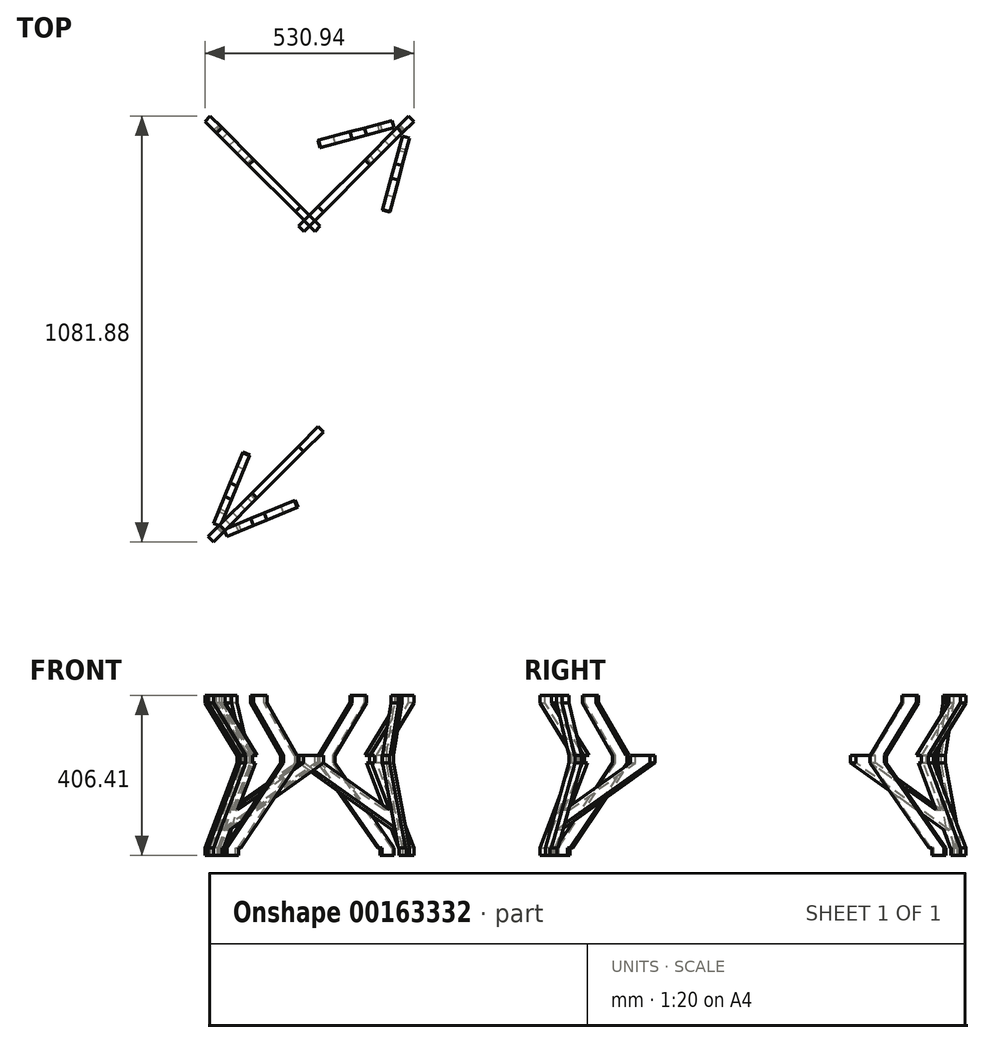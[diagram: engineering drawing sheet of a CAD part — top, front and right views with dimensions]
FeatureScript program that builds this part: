
annotation { "Feature Type Name" : "Feature", "Feature Type Description" : "" }
export const myFeature = defineFeature(function(context is Context, id is Id, definition is map)
    precondition{}
    {
        {
            var Q0;
            Q0=qCreatedBy(makeId("Top.planeOp"),FACE);
            var sketch = newSketch(context, id + "F0", { "sketchPlane" : qUnion([Q0])});
            skLineSegment(sketch, "E0.bottom", {"start": v(0, 1117.6) * mm, "end": v(558.8, 1117.6) * mm});
            skLineSegment(sketch, "E0.top", {"start": v(0, 0) * mm, "end": v(558.8, 0) * mm});
            skLineSegment(sketch, "E0.left", {"start": v(0, 1117.6) * mm, "end": v(0, 0) * mm});
            skLineSegment(sketch, "E0.right", {"start": v(558.8, 1117.6) * mm, "end": v(558.8, 0) * mm});
            skLineSegment(sketch, "E1", {"start": v(0, 0) * mm, "end": v(425.13, 425.13) * mm, "construction": true});
            skLineSegment(sketch, "E2", {"start": v(0, 1117.6) * mm, "end": v(422.37, 695.23) * mm, "construction": true});
            skLineSegment(sketch, "E3", {"start": v(558.8, 1117.6) * mm, "end": v(139.7, 698.5) * mm, "construction": true});
            skLineSegment(sketch, "E4", {"start": v(0, 1117.6) * mm, "end": v(139.7, 1117.6) * mm});
            skLineSegment(sketch, "E5", {"start": v(139.7, 1117.6) * mm, "end": v(139.7, 0) * mm, "construction": true});
            skLineSegment(sketch, "E6", {"start": v(558.8, 0) * mm, "end": v(419.1, 0) * mm});
            skLineSegment(sketch, "E7", {"start": v(558.8, 0) * mm, "end": v(436.13, 32.87) * mm});
            skLineSegment(sketch, "E8", {"start": v(558.8, 0) * mm, "end": v(525.93, 122.67) * mm});
            skLineSegment(sketch, "E9", {"start": v(436.13, 32.87) * mm, "end": v(525.93, 122.67) * mm});
            skLineSegment(sketch, "E10", {"start": v(525.93, 122.67) * mm, "end": v(497.46, 16.44) * mm, "construction": true});
            skLineSegment(sketch, "E11", {"start": v(436.13, 32.87) * mm, "end": v(542.37, 61.34) * mm, "construction": true});
            skLineSegment(sketch, "E12", {"start": v(558.8, 0) * mm, "end": v(540.82, 17.98) * mm});
            skLineSegment(sketch, "E13", {"start": v(511.63, 33.7) * mm, "end": v(525.1, 47.17) * mm});
            skLineSegment(sketch, "E14", {"start": v(525.1, 47.17) * mm, "end": v(547.55, 24.72) * mm});
            skLineSegment(sketch, "E15", {"start": v(547.55, 24.72) * mm, "end": v(534.08, 11.25) * mm});
            skLineSegment(sketch, "E16", {"start": v(534.08, 11.25) * mm, "end": v(511.63, 33.7) * mm});
            skLineSegment(sketch, "E17", {"start": v(436.13, 32.87) * mm, "end": v(460.66, 39.44) * mm});
            skLineSegment(sketch, "E18", {"start": v(460.66, 39.44) * mm, "end": v(458.2, 48.65) * mm});
            skLineSegment(sketch, "E19", {"start": v(458.2, 48.65) * mm, "end": v(488.86, 56.87) * mm});
            skLineSegment(sketch, "E20", {"start": v(488.86, 56.87) * mm, "end": v(493.8, 38.46) * mm});
            skLineSegment(sketch, "E21", {"start": v(493.8, 38.46) * mm, "end": v(463.12, 30.25) * mm});
            skLineSegment(sketch, "E22", {"start": v(460.66, 39.44) * mm, "end": v(463.12, 30.25) * mm});
            skLineSegment(sketch, "E23", {"start": v(525.93, 122.67) * mm, "end": v(519.36, 98.14) * mm});
            skLineSegment(sketch, "E24", {"start": v(510.15, 100.61) * mm, "end": v(528.56, 95.68) * mm});
            skLineSegment(sketch, "E25", {"start": v(528.56, 95.68) * mm, "end": v(520.34, 65) * mm});
            skLineSegment(sketch, "E26", {"start": v(520.34, 65) * mm, "end": v(501.93, 69.94) * mm});
            skLineSegment(sketch, "E27", {"start": v(501.93, 69.94) * mm, "end": v(510.15, 100.61) * mm});
            skLineSegment(sketch, "E28", {"start": v(558.8, 0) * mm, "end": v(139.7, 419.1) * mm, "construction": true});
            skLineSegment(sketch, "E29", {"start": v(558.8, 1117.6) * mm, "end": v(436.13, 1084.73) * mm});
            skLineSegment(sketch, "E30", {"start": v(558.8, 1117.6) * mm, "end": v(525.93, 994.93) * mm});
            skLineSegment(sketch, "E31", {"start": v(436.13, 1084.73) * mm, "end": v(525.93, 994.93) * mm});
            skLineSegment(sketch, "E32", {"start": v(544.69, 1090.11) * mm, "end": v(531.22, 1103.59) * mm});
            skLineSegment(sketch, "E33", {"start": v(531.22, 1103.59) * mm, "end": v(508.77, 1081.14) * mm});
            skLineSegment(sketch, "E34", {"start": v(508.77, 1081.14) * mm, "end": v(522.24, 1067.66) * mm});
            skLineSegment(sketch, "E35", {"start": v(522.24, 1067.66) * mm, "end": v(544.69, 1090.11) * mm});
            skLineSegment(sketch, "E36.0", {"start": v(551.72, 1115.7) * mm, "end": v(520.75, 1000.11) * mm, "construction": true});
            skLineSegment(sketch, "E37.0", {"start": v(443.2, 1086.63) * mm, "end": v(527.83, 1002) * mm, "construction": true});
            skLineSegment(sketch, "E38.trimOffspring", {"start": v(556.9, 1110.52) * mm, "end": v(441.31, 1079.55) * mm, "construction": true});
            skLineSegment(sketch, "E39", {"start": v(525.5, 1017.82) * mm, "end": v(507.09, 1022.75) * mm});
            skLineSegment(sketch, "E40", {"start": v(507.09, 1022.75) * mm, "end": v(515.3, 1053.41) * mm});
            skLineSegment(sketch, "E41", {"start": v(515.3, 1053.41) * mm, "end": v(533.7, 1048.48) * mm});
            skLineSegment(sketch, "E42", {"start": v(533.7, 1048.48) * mm, "end": v(525.5, 1017.82) * mm});
            skLineSegment(sketch, "E43", {"start": v(459, 1084.29) * mm, "end": v(463.94, 1065.9) * mm});
            skLineSegment(sketch, "E44", {"start": v(463.94, 1065.9) * mm, "end": v(494.6, 1074.11) * mm});
            skLineSegment(sketch, "E45", {"start": v(494.6, 1074.11) * mm, "end": v(489.68, 1092.5) * mm});
            skLineSegment(sketch, "E46", {"start": v(489.68, 1092.5) * mm, "end": v(459, 1084.29) * mm});
            skPoint(sketch, "E47", {"position": v(492.14, 1083.3) * mm});
            skPoint(sketch, "E48", {"position": v(524.5, 1050.95) * mm});
            skLineSegment(sketch, "E49", {"start": v(492.14, 1083.3) * mm, "end": v(139.7, 988.87) * mm, "construction": true});
            skLineSegment(sketch, "E50", {"start": v(516.29, 1020.29) * mm, "end": v(422.56, 670.5) * mm, "construction": true});
            skPoint(sketch, "E51.orphan", {"position": v(461.47, 1075.1) * mm});
            skLineSegment(sketch, "E52", {"start": v(0, 1117.6) * mm, "end": v(32.87, 994.93) * mm});
            skLineSegment(sketch, "E53", {"start": v(0, 1117.6) * mm, "end": v(122.67, 1084.73) * mm});
            skLineSegment(sketch, "E54", {"start": v(122.67, 1084.73) * mm, "end": v(32.87, 994.93) * mm});
            skLineSegment(sketch, "E55.0", {"start": v(6.57, 1117.6) * mm, "end": v(38.05, 1000.11) * mm, "construction": true});
            skLineSegment(sketch, "E56.0", {"start": v(0, 1111.03) * mm, "end": v(117.49, 1079.55) * mm, "construction": true});
            skLineSegment(sketch, "E57.0", {"start": v(115.6, 1086.63) * mm, "end": v(30.97, 1002) * mm, "construction": true});
            skLineSegment(sketch, "E58", {"start": v(33.3, 1017.85) * mm, "end": v(51.7, 1022.78) * mm});
            skLineSegment(sketch, "E59", {"start": v(51.7, 1022.78) * mm, "end": v(43.49, 1053.45) * mm});
            skLineSegment(sketch, "E60", {"start": v(43.49, 1053.45) * mm, "end": v(25.09, 1048.51) * mm});
            skLineSegment(sketch, "E61", {"start": v(25.09, 1048.51) * mm, "end": v(33.3, 1017.85) * mm});
            skLineSegment(sketch, "E62", {"start": v(99.77, 1084.3) * mm, "end": v(94.84, 1065.9) * mm});
            skLineSegment(sketch, "E63", {"start": v(94.84, 1065.9) * mm, "end": v(64.18, 1074.1) * mm});
            skLineSegment(sketch, "E64", {"start": v(64.18, 1074.1) * mm, "end": v(69.11, 1092.5) * mm});
            skLineSegment(sketch, "E65", {"start": v(69.11, 1092.5) * mm, "end": v(99.77, 1084.3) * mm});
            skPoint(sketch, "E66", {"position": v(66.65, 1083.3) * mm});
            skPoint(sketch, "E67", {"position": v(34.29, 1050.98) * mm});
            skLineSegment(sketch, "E68", {"start": v(66.65, 1083.3) * mm, "end": v(420.1, 988.6) * mm, "construction": true});
            skLineSegment(sketch, "E69", {"start": v(34.29, 1050.98) * mm, "end": v(139.7, 657.57) * mm, "construction": true});
            skPoint(sketch, "E70", {"position": v(419.1, 1117.6) * mm});
            skLineSegment(sketch, "E71", {"start": v(419.1, 1117.6) * mm, "end": v(427.75, 0) * mm, "construction": true});
            skLineSegment(sketch, "E72.MirrorCS", {"start": v(59.37, 1058.23) * mm, "end": v(-363, 1480.6) * mm, "construction": true});
            skLineSegment(sketch, "E73", {"start": v(27.38, 1103.69) * mm, "end": v(13.91, 1090.22) * mm});
            skLineSegment(sketch, "E74", {"start": v(13.91, 1090.22) * mm, "end": v(36.36, 1067.77) * mm});
            skLineSegment(sketch, "E75", {"start": v(36.36, 1067.77) * mm, "end": v(49.83, 1081.24) * mm});
            skLineSegment(sketch, "E76", {"start": v(27.38, 1103.69) * mm, "end": v(49.83, 1081.24) * mm});
            skLineSegment(sketch, "E77", {"start": v(0, 0) * mm, "end": v(48.6, 117.33) * mm});
            skLineSegment(sketch, "E78", {"start": v(0, 0) * mm, "end": v(117.33, 48.6) * mm});
            skPoint(sketch, "E79", {"position": v(117.33, 48.6) * mm});
            skPoint(sketch, "E80", {"position": v(48.6, 117.33) * mm});
            skLineSegment(sketch, "E81", {"start": v(48.6, 117.33) * mm, "end": v(117.33, 48.6) * mm});
            skLineSegment(sketch, "E82.0", {"start": v(5.87, -2.43) * mm, "end": v(54.47, 114.9) * mm, "construction": true});
            skLineSegment(sketch, "E83.0", {"start": v(-2.43, 5.87) * mm, "end": v(114.9, 54.47) * mm, "construction": true});
            skLineSegment(sketch, "E84", {"start": v(21.83, 35.3) * mm, "end": v(44.28, 57.75) * mm});
            skLineSegment(sketch, "E85", {"start": v(35.3, 21.83) * mm, "end": v(57.75, 44.28) * mm});
            skLineSegment(sketch, "E86", {"start": v(44.28, 57.75) * mm, "end": v(57.75, 44.28) * mm});
            skLineSegment(sketch, "E87", {"start": v(21.83, 35.3) * mm, "end": v(35.3, 21.83) * mm});
            skLineSegment(sketch, "E88.0", {"start": v(44.11, 112.84) * mm, "end": v(112.84, 44.11) * mm, "construction": true});
            skLineSegment(sketch, "E89", {"start": v(47.74, 98.66) * mm, "end": v(65.34, 91.37) * mm});
            skLineSegment(sketch, "E90", {"start": v(65.34, 91.37) * mm, "end": v(53.2, 62.04) * mm});
            skLineSegment(sketch, "E91", {"start": v(53.2, 62.04) * mm, "end": v(35.6, 69.33) * mm});
            skLineSegment(sketch, "E92", {"start": v(35.6, 69.33) * mm, "end": v(47.74, 98.66) * mm});
            skLineSegment(sketch, "E93", {"start": v(98.94, 47.85) * mm, "end": v(91.65, 65.45) * mm});
            skLineSegment(sketch, "E94", {"start": v(91.65, 65.45) * mm, "end": v(62.3, 53.3) * mm});
            skLineSegment(sketch, "E95", {"start": v(62.3, 53.3) * mm, "end": v(69.6, 35.7) * mm});
            skLineSegment(sketch, "E96", {"start": v(69.6, 35.7) * mm, "end": v(98.94, 47.85) * mm});
            skPoint(sketch, "E97", {"position": v(65.95, 44.5) * mm});
            skLineSegment(sketch, "E98", {"start": v(95.3, 56.65) * mm, "end": v(426.25, 193.74) * mm, "construction": true});
            skPoint(sketch, "E99", {"position": v(44.4, 65.69) * mm});
            skLineSegment(sketch, "E100", {"start": v(44.4, 65.69) * mm, "end": v(139.7, 295.78) * mm, "construction": true});
            skPoint(sketch, "E101.orphan", {"position": v(56.54, 95.02) * mm});
            skSolve(sketch);
        }
        {
            var Q0;
            Q0=sQuery(id+"F0.wireOp",EDGE,"E1");
            var Q1;
            {var subQ1=sQuery(id+"F0.wireOp",EDGE,"E1");var subQ7=sQuery(id+"F0.wireOp",EDGE,"E5");var subQ9=makeQuery(id+"F0.imprint","INTERSECT",VERTEX,{"derivedFrom":[subQ1,subQ7]});Q1=makeQuery(id+"F0.imprint","IMPRINT",FACE,{"disambiguationData":[TD([[makeQuery(id+"F0.imprint","IMPRINT",EDGE,{"disambiguationData":[TD([[subQ9,-1.0]])],"derivedFrom":subQ1}),-1.0]])]});}
            cPlane(context, id + "F1", {"entities" : qUnion([Q0, Q1]), "cplaneType" : CPlaneType.LINE_ANGLE, "offset" : 25.4 * mm, "angle" : 90 * degree, "width" : 152.4 * mm, "height" : 152.4 * mm});
        }
        {
            var Q0;
            Q0=sQuery(id+"F0.wireOp",EDGE,"E3");
            var Q1;
            {var subQ0=sQuery(id+"F0.wireOp",EDGE,"E5");var subQ1=sQuery(id+"F0.wireOp",EDGE,"E2");var subQ2=makeQuery(id+"F0.imprint","INTERSECT",VERTEX,{"derivedFrom":[subQ1,subQ0]});Q1=makeQuery(id+"F0.imprint","IMPRINT",FACE,{"disambiguationData":[TD([[makeQuery(id+"F0.imprint","IMPRINT",EDGE,{"disambiguationData":[TD([[subQ2,-1.0]])],"derivedFrom":subQ1}),-1.0]])]});}
            cPlane(context, id + "F2", {"entities" : qUnion([Q0, Q1]), "cplaneType" : CPlaneType.LINE_ANGLE, "offset" : 25.4 * mm, "angle" : 90 * degree, "width" : 152.4 * mm, "height" : 152.4 * mm});
        }
        {
            var Q0;
            Q0=qCreatedBy(id+"F2.planeOp",FACE);
            var sketch = newSketch(context, id + "F3", { "sketchPlane" : qUnion([Q0])});
            skLineSegment(sketch, "E102", {"start": v(1156.11, 0) * mm, "end": v(1156.11, 406.4) * mm, "construction": true});
            skLineSegment(sketch, "E103", {"start": v(592.65, 0) * mm, "end": v(592.65, 406.4) * mm, "construction": true});
            skLineSegment(sketch, "E104", {"start": v(1156.11, 406.4) * mm, "end": v(592.65, 406.4) * mm, "construction": true});
            skLineSegment(sketch, "E105.0", {"start": v(1156.11, 387.35) * mm, "end": v(592.65, 387.35) * mm, "construction": true});
            skPoint(sketch, "E106", {"position": v(1156.11, 254) * mm});
            skLineSegment(sketch, "E107", {"start": v(1156.11, 254) * mm, "end": v(592.65, 254) * mm, "construction": true});
            skLineSegment(sketch, "E108.0", {"start": v(1156.11, 234.95) * mm, "end": v(1040.74, 234.95) * mm, "construction": true});
            skLineSegment(sketch, "E109", {"start": v(1124.36, 0) * mm, "end": v(592.65, 0) * mm, "construction": true});
            skLineSegment(sketch, "E110.0", {"start": v(1120, 19.05) * mm, "end": v(592.65, 19.05) * mm, "construction": true});
            skLineSegment(sketch, "E111", {"start": v(1156.11, 19.05) * mm, "end": v(1040.74, 234.95) * mm});
            skLineSegment(sketch, "E112", {"start": v(1124.36, 19.05) * mm, "end": v(1124.36, 0) * mm});
            skLineSegment(sketch, "E113", {"start": v(1120, 19.05) * mm, "end": v(1094.73, 66.36) * mm});
            skLineSegment(sketch, "E114", {"start": v(1040.74, 234.95) * mm, "end": v(1040.74, 254) * mm});
            skLineSegment(sketch, "E115", {"start": v(1040.74, 254) * mm, "end": v(1156.11, 387.35) * mm});
            skLineSegment(sketch, "E116", {"start": v(1124.36, 19.05) * mm, "end": v(1120, 19.05) * mm});
            skLineSegment(sketch, "E117.0", {"start": v(998.76, 254) * mm, "end": v(1114.13, 387.35) * mm});
            skLineSegment(sketch, "E118", {"start": v(1015.34, 234.95) * mm, "end": v(1015.34, 254) * mm});
            skLineSegment(sketch, "E119", {"start": v(1015.34, 254) * mm, "end": v(998.76, 254) * mm});
            skLineSegment(sketch, "E120", {"start": v(1015.34, 234.95) * mm, "end": v(1004.64, 234.95) * mm});
            skLineSegment(sketch, "E121", {"start": v(1094.73, 66.36) * mm, "end": v(760.94, 234.95) * mm});
            skLineSegment(sketch, "E122.0", {"start": v(1068.7, 115.08) * mm, "end": v(831.36, 234.95) * mm});
            skLineSegment(sketch, "E123.trimOffspring", {"start": v(1068.7, 115.08) * mm, "end": v(1004.64, 234.95) * mm});
            skLineSegment(sketch, "E124", {"start": v(790.12, 0) * mm, "end": v(779.62, 406.4) * mm, "construction": true});
            skLineSegment(sketch, "E125", {"start": v(760.94, 234.95) * mm, "end": v(760.94, 254) * mm});
            skLineSegment(sketch, "E126", {"start": v(831.36, 234.95) * mm, "end": v(831.36, 254) * mm});
            skLineSegment(sketch, "E127", {"start": v(831.36, 254) * mm, "end": v(760.94, 254) * mm});
            skLineSegment(sketch, "E128", {"start": v(1004.64, 234.95) * mm, "end": v(1015.34, 234.95) * mm});
            skLineSegment(sketch, "E129.trimOffspring", {"start": v(1015.34, 234.95) * mm, "end": v(592.65, 234.95) * mm, "construction": true});
            skLineSegment(sketch, "E130", {"start": v(1156.11, 19.05) * mm, "end": v(1156.11, 0) * mm});
            skLineSegment(sketch, "E131", {"start": v(1156.11, 0) * mm, "end": v(1124.36, 0) * mm});
            skLineSegment(sketch, "E132", {"start": v(1114.13, 387.35) * mm, "end": v(1114.13, 406.4) * mm});
            skLineSegment(sketch, "E133", {"start": v(1114.13, 406.4) * mm, "end": v(1156.11, 406.4) * mm});
            skLineSegment(sketch, "E134", {"start": v(1156.11, 387.35) * mm, "end": v(1156.11, 406.4) * mm});
            skSolve(sketch);
        }
        {
            var Q0;
            Q0=sQuery(id+"F0.wireOp",EDGE,"E49");
            cPlane(context, id + "F4", {"entities" : qUnion([Q0]), "cplaneType" : CPlaneType.LINE_ANGLE, "offset" : 25.4 * mm, "angle" : 180 * degree, "width" : 152.4 * mm, "height" : 152.4 * mm});
        }
        {
            var Q0;
            Q0=qCreatedBy(id+"F4.planeOp",FACE);
            var sketch = newSketch(context, id + "F5", { "sketchPlane" : qUnion([Q0])});
            skLineSegment(sketch, "E135", {"start": v(-755.76, 0) * mm, "end": v(-755.76, 406.4) * mm, "construction": true});
            skLineSegment(sketch, "E136", {"start": v(-390.89, 0) * mm, "end": v(-390.89, 406.4) * mm, "construction": true});
            skLineSegment(sketch, "E137", {"start": v(-535.5, 0) * mm, "end": v(-535.5, 406.4) * mm, "construction": true});
            skLineSegment(sketch, "E138", {"start": v(-755.76, 406.4) * mm, "end": v(-682.75, 406.4) * mm, "construction": true});
            skLineSegment(sketch, "E139", {"start": v(-755.76, 254) * mm, "end": v(-390.89, 254) * mm, "construction": true});
            skLineSegment(sketch, "E140", {"start": v(-755.76, 0) * mm, "end": v(-390.89, 0) * mm, "construction": true});
            skLineSegment(sketch, "E141.0", {"start": v(-755.76, 387.35) * mm, "end": v(-390.89, 387.35) * mm, "construction": true});
            skLineSegment(sketch, "E142.0", {"start": v(-803.66, 234.95) * mm, "end": v(-315.69, 234.95) * mm, "construction": true});
            skLineSegment(sketch, "E143", {"start": v(-755.76, 0) * mm, "end": v(-724.01, 0) * mm});
            skLineSegment(sketch, "E144", {"start": v(-724.01, 0) * mm, "end": v(-724.01, 19.05) * mm});
            skLineSegment(sketch, "E145", {"start": v(-755.76, 19.05) * mm, "end": v(-755.76, 0) * mm});
            skLineSegment(sketch, "E146", {"start": v(-755.76, 19.05) * mm, "end": v(-599.6, 234.95) * mm});
            skLineSegment(sketch, "E147.0", {"start": v(-716.58, 19.05) * mm, "end": v(-560.41, 234.95) * mm});
            skLineSegment(sketch, "E148", {"start": v(-724.01, 19.05) * mm, "end": v(-716.58, 19.05) * mm});
            skLineSegment(sketch, "E149", {"start": v(-599.6, 234.95) * mm, "end": v(-599.6, 254) * mm});
            skLineSegment(sketch, "E150", {"start": v(-560.41, 234.95) * mm, "end": v(-560.41, 254) * mm});
            skLineSegment(sketch, "E151", {"start": v(-599.6, 254) * mm, "end": v(-682.75, 387.35) * mm});
            skLineSegment(sketch, "E152.0", {"start": v(-562.18, 254) * mm, "end": v(-645.33, 387.35) * mm});
            skLineSegment(sketch, "E153", {"start": v(-682.75, 387.35) * mm, "end": v(-682.75, 406.4) * mm});
            skLineSegment(sketch, "E154", {"start": v(-645.33, 387.35) * mm, "end": v(-645.33, 406.4) * mm});
            skLineSegment(sketch, "E155.trimOffspring", {"start": v(-639.62, 406.4) * mm, "end": v(-390.89, 406.4) * mm, "construction": true});
            skLineSegment(sketch, "E156", {"start": v(-682.75, 406.4) * mm, "end": v(-645.33, 406.4) * mm});
            skLineSegment(sketch, "E157", {"start": v(-562.18, 254) * mm, "end": v(-560.41, 254) * mm});
            skSolve(sketch);
        }
        {
            var Q0;
            Q0=makeQuery(id+"F3.imprint","IMPRINT",FACE,{"disambiguationData":[TD([[makeQuery(id+"F3.imprint","IMPRINT",EDGE,{"derivedFrom":sQuery(id+"F3.wireOp",EDGE,"E111")}),1.0]])]});
            extrude(context, id + "F6", {"entities" : qUnion([Q0]), "endBound" : BoundingType.SYMMETRIC, "depth" : 19.05 * mm});
        }
        {
            var Q0;
            Q0=makeQuery(id+"F5.imprint","IMPRINT",FACE,{"disambiguationData":[TD([[makeQuery(id+"F5.imprint","IMPRINT",EDGE,{"derivedFrom":sQuery(id+"F5.wireOp",EDGE,"E143")}),1.0]])]});
            extrude(context, id + "F7", {"entities" : qUnion([Q0]), "endBound" : BoundingType.SYMMETRIC, "depth" : 19.05 * mm});
        }
        {
            var Q0;
            Q0=sQuery(id+"F0.wireOp",EDGE,"E50");
            cPlane(context, id + "F8", {"entities" : qUnion([Q0]), "cplaneType" : CPlaneType.LINE_ANGLE, "offset" : 25.4 * mm, "angle" : 90 * degree, "width" : 152.4 * mm, "height" : 152.4 * mm});
        }
        {
            var Q0;
            Q0=qCreatedBy(id+"F8.planeOp",FACE);
            var sketch = newSketch(context, id + "F9", { "sketchPlane" : qUnion([Q0])});
            skLineSegment(sketch, "E158", {"start": v(786.02, 0) * mm, "end": v(786.02, 406.4) * mm, "construction": true});
            skLineSegment(sketch, "E159.MirrorCS", {"start": v(957.31, 254) * mm, "end": v(955.54, 254) * mm});
            skLineSegment(sketch, "E160.MirrorCS", {"start": v(1119.14, 19.06) * mm, "end": v(1111.7, 19.06) * mm});
            skLineSegment(sketch, "E161.MirrorCS", {"start": v(1150.9, 19.06) * mm, "end": v(1150.9, 0) * mm});
            skLineSegment(sketch, "E162.MirrorCS", {"start": v(1119.14, 0) * mm, "end": v(1119.14, 19.06) * mm});
            skLineSegment(sketch, "E163.MirrorCS", {"start": v(1150.9, 0) * mm, "end": v(1119.14, 0) * mm});
            skLineSegment(sketch, "E164.MirrorCS", {"start": v(1034.75, 406.4) * mm, "end": v(786.02, 406.4) * mm, "construction": true});
            skLineSegment(sketch, "E165.MirrorCS", {"start": v(994.73, 254) * mm, "end": v(1077.87, 387.36) * mm});
            skLineSegment(sketch, "E166.MirrorCS", {"start": v(1077.87, 387.36) * mm, "end": v(1077.87, 406.4) * mm});
            skLineSegment(sketch, "E167.MirrorCS", {"start": v(1111.7, 19.06) * mm, "end": v(955.54, 234.96) * mm});
            skLineSegment(sketch, "E168.MirrorCS", {"start": v(1150.9, 19.06) * mm, "end": v(994.73, 234.96) * mm});
            skLineSegment(sketch, "E169.MirrorCS", {"start": v(1040.46, 387.36) * mm, "end": v(1040.46, 406.4) * mm});
            skLineSegment(sketch, "E170.MirrorCS", {"start": v(1150.9, 234.96) * mm, "end": v(786.02, 234.96) * mm, "construction": true});
            skLineSegment(sketch, "E171.MirrorCS", {"start": v(1077.87, 406.4) * mm, "end": v(1040.46, 406.4) * mm});
            skLineSegment(sketch, "E172.MirrorCS", {"start": v(1150.9, 387.36) * mm, "end": v(786.02, 387.36) * mm, "construction": true});
            skLineSegment(sketch, "E173.MirrorCS", {"start": v(1150.9, 0) * mm, "end": v(786.02, 0) * mm, "construction": true});
            skLineSegment(sketch, "E174.MirrorCS", {"start": v(1150.9, 254) * mm, "end": v(786.02, 254) * mm, "construction": true});
            skLineSegment(sketch, "E175.MirrorCS", {"start": v(1150.9, 406.4) * mm, "end": v(1077.87, 406.4) * mm, "construction": true});
            skLineSegment(sketch, "E176.MirrorCS", {"start": v(1150.9, 0) * mm, "end": v(1150.9, 406.4) * mm, "construction": true});
            skLineSegment(sketch, "E177.MirrorCS", {"start": v(930.63, 0) * mm, "end": v(930.63, 406.4) * mm, "construction": true});
            skLineSegment(sketch, "E178.MirrorCS", {"start": v(955.54, 234.96) * mm, "end": v(955.54, 254) * mm});
            skLineSegment(sketch, "E179.MirrorCS", {"start": v(994.73, 234.96) * mm, "end": v(994.73, 254) * mm});
            skLineSegment(sketch, "E180.MirrorCS", {"start": v(957.31, 254) * mm, "end": v(1040.46, 387.36) * mm});
            skSolve(sketch);
        }
        {
            var Q0;
            Q0=makeQuery(id+"F9.imprint","IMPRINT",FACE,{"disambiguationData":[TD([[makeQuery(id+"F9.imprint","IMPRINT",EDGE,{"derivedFrom":sQuery(id+"F9.wireOp",EDGE,"E159.MirrorCS")}),1.0]])]});
            extrude(context, id + "F10", {"entities" : qUnion([Q0]), "endBound" : BoundingType.SYMMETRIC, "depth" : 19.05 * mm});
        }
        {
            var Q0;
            Q0=sQuery(id+"F0.wireOp",EDGE,"E2");
            cPlane(context, id + "F11", {"entities" : qUnion([Q0]), "cplaneType" : CPlaneType.LINE_ANGLE, "offset" : 25.4 * mm, "angle" : 90 * degree, "width" : 152.4 * mm, "height" : 152.4 * mm});
        }
        {
            var Q0;
            Q0=qCreatedBy(id+"F11.planeOp",FACE);
            var sketch = newSketch(context, id + "F12", { "sketchPlane" : qUnion([Q0])});
            skLineSegment(sketch, "E181", {"start": v(761.1, 0) * mm, "end": v(761.1, 406.4) * mm, "construction": true});
            skLineSegment(sketch, "E182", {"start": v(197.63, 0) * mm, "end": v(197.63, 406.4) * mm, "construction": true});
            skLineSegment(sketch, "E183", {"start": v(761.1, 406.4) * mm, "end": v(197.63, 406.4) * mm, "construction": true});
            skLineSegment(sketch, "E184.0", {"start": v(761.1, 387.35) * mm, "end": v(197.63, 387.35) * mm, "construction": true});
            skPoint(sketch, "E185", {"position": v(761.1, 254) * mm});
            skLineSegment(sketch, "E186", {"start": v(761.1, 254) * mm, "end": v(197.63, 254) * mm, "construction": true});
            skLineSegment(sketch, "E187.0", {"start": v(761.1, 234.95) * mm, "end": v(645.72, 234.95) * mm, "construction": true});
            skLineSegment(sketch, "E188", {"start": v(729.34, 0) * mm, "end": v(197.63, 0) * mm, "construction": true});
            skLineSegment(sketch, "E189.0", {"start": v(724.99, 19.05) * mm, "end": v(197.63, 19.05) * mm, "construction": true});
            skLineSegment(sketch, "E190", {"start": v(761.1, 19.05) * mm, "end": v(645.72, 234.95) * mm});
            skLineSegment(sketch, "E191", {"start": v(729.34, 19.05) * mm, "end": v(729.34, 0) * mm});
            skLineSegment(sketch, "E192", {"start": v(724.99, 19.05) * mm, "end": v(699.7, 66.36) * mm});
            skLineSegment(sketch, "E193", {"start": v(645.72, 234.95) * mm, "end": v(645.72, 254) * mm});
            skLineSegment(sketch, "E194", {"start": v(645.72, 254) * mm, "end": v(761.1, 387.35) * mm});
            skLineSegment(sketch, "E195", {"start": v(729.34, 19.05) * mm, "end": v(724.99, 19.05) * mm});
            skLineSegment(sketch, "E196.0", {"start": v(603.73, 254) * mm, "end": v(719.1, 387.35) * mm});
            skLineSegment(sketch, "E197", {"start": v(620.32, 234.95) * mm, "end": v(620.32, 254) * mm});
            skLineSegment(sketch, "E198", {"start": v(620.32, 254) * mm, "end": v(603.73, 254) * mm});
            skLineSegment(sketch, "E199", {"start": v(620.32, 234.95) * mm, "end": v(609.61, 234.95) * mm});
            skLineSegment(sketch, "E200", {"start": v(699.7, 66.36) * mm, "end": v(365.91, 234.95) * mm});
            skLineSegment(sketch, "E201.0", {"start": v(673.67, 115.08) * mm, "end": v(436.34, 234.95) * mm});
            skLineSegment(sketch, "E202.trimOffspring", {"start": v(673.67, 115.08) * mm, "end": v(609.61, 234.95) * mm});
            skLineSegment(sketch, "E203", {"start": v(395.1, 0) * mm, "end": v(384.6, 406.4) * mm, "construction": true});
            skLineSegment(sketch, "E204", {"start": v(365.91, 234.95) * mm, "end": v(365.91, 254) * mm});
            skLineSegment(sketch, "E205", {"start": v(436.34, 234.95) * mm, "end": v(436.34, 254) * mm});
            skLineSegment(sketch, "E206", {"start": v(436.34, 254) * mm, "end": v(365.91, 254) * mm});
            skLineSegment(sketch, "E207", {"start": v(609.61, 234.95) * mm, "end": v(620.32, 234.95) * mm});
            skLineSegment(sketch, "E208.trimOffspring", {"start": v(620.32, 234.95) * mm, "end": v(197.63, 234.95) * mm, "construction": true});
            skLineSegment(sketch, "E209", {"start": v(761.1, 19.05) * mm, "end": v(761.1, 0) * mm});
            skLineSegment(sketch, "E210", {"start": v(761.1, 0) * mm, "end": v(729.34, 0) * mm});
            skLineSegment(sketch, "E211", {"start": v(719.1, 387.35) * mm, "end": v(719.1, 406.4) * mm});
            skLineSegment(sketch, "E212", {"start": v(719.1, 406.4) * mm, "end": v(761.1, 406.4) * mm});
            skLineSegment(sketch, "E213", {"start": v(761.1, 387.35) * mm, "end": v(761.1, 406.4) * mm});
            skSolve(sketch);
        }
        {
            var Q0;
            Q0=makeQuery(id+"F12.imprint","IMPRINT",FACE,{"disambiguationData":[TD([[makeQuery(id+"F12.imprint","IMPRINT",EDGE,{"derivedFrom":sQuery(id+"F12.wireOp",EDGE,"E190")}),1.0]])]});
            extrude(context, id + "F13", {"entities" : qUnion([Q0]), "endBound" : BoundingType.SYMMETRIC, "depth" : 19.05 * mm});
        }
        {
            var Q0;
            Q0=qCreatedBy(id+"F1.planeOp",FACE);
            var sketch = newSketch(context, id + "F14", { "sketchPlane" : qUnion([Q0])});
            skLineSegment(sketch, "E214", {"start": v(603.86, 0) * mm, "end": v(603.86, 406.4) * mm, "construction": true});
            skLineSegment(sketch, "E215.MirrorCS", {"start": v(191.87, 234.95) * mm, "end": v(181.17, 234.95) * mm});
            skLineSegment(sketch, "E216.MirrorCS", {"start": v(72.14, 19.05) * mm, "end": v(76.5, 19.05) * mm});
            skLineSegment(sketch, "E217.MirrorCS", {"start": v(181.17, 234.95) * mm, "end": v(191.87, 234.95) * mm});
            skLineSegment(sketch, "E218.MirrorCS", {"start": v(40.4, 387.35) * mm, "end": v(40.4, 406.4) * mm});
            skLineSegment(sketch, "E219.MirrorCS", {"start": v(40.4, 19.05) * mm, "end": v(40.4, 0) * mm});
            skLineSegment(sketch, "E220.MirrorCS", {"start": v(181.17, 254) * mm, "end": v(197.75, 254) * mm});
            skLineSegment(sketch, "E221.MirrorCS", {"start": v(365.15, 254) * mm, "end": v(435.57, 254) * mm});
            skLineSegment(sketch, "E222.MirrorCS", {"start": v(82.38, 406.4) * mm, "end": v(40.4, 406.4) * mm});
            skLineSegment(sketch, "E223.MirrorCS", {"start": v(40.4, 387.35) * mm, "end": v(603.86, 387.35) * mm, "construction": true});
            skLineSegment(sketch, "E224.MirrorCS", {"start": v(127.81, 115.08) * mm, "end": v(191.87, 234.95) * mm});
            skLineSegment(sketch, "E225.MirrorCS", {"start": v(40.4, 406.4) * mm, "end": v(603.86, 406.4) * mm, "construction": true});
            skLineSegment(sketch, "E226.MirrorCS", {"start": v(435.57, 234.95) * mm, "end": v(435.57, 254) * mm});
            skLineSegment(sketch, "E227.MirrorCS", {"start": v(40.4, 0) * mm, "end": v(40.4, 406.4) * mm, "construction": true});
            skPoint(sketch, "E228.MirrorP", {"position": v(40.4, 254) * mm});
            skLineSegment(sketch, "E229.MirrorCS", {"start": v(181.17, 234.95) * mm, "end": v(181.17, 254) * mm});
            skLineSegment(sketch, "E230.MirrorCS", {"start": v(197.75, 254) * mm, "end": v(82.38, 387.35) * mm});
            skLineSegment(sketch, "E231.MirrorCS", {"start": v(101.78, 66.36) * mm, "end": v(435.57, 234.95) * mm});
            skLineSegment(sketch, "E232.MirrorCS", {"start": v(82.38, 387.35) * mm, "end": v(82.38, 406.4) * mm});
            skLineSegment(sketch, "E233.MirrorCS", {"start": v(181.17, 234.95) * mm, "end": v(603.86, 234.95) * mm, "construction": true});
            skLineSegment(sketch, "E234.MirrorCS", {"start": v(406.4, 0) * mm, "end": v(416.88, 406.4) * mm, "construction": true});
            skLineSegment(sketch, "E235.MirrorCS", {"start": v(40.4, 0) * mm, "end": v(72.14, 0) * mm});
            skLineSegment(sketch, "E236.MirrorCS", {"start": v(127.81, 115.08) * mm, "end": v(365.15, 234.95) * mm});
            skLineSegment(sketch, "E237.MirrorCS", {"start": v(365.15, 234.95) * mm, "end": v(365.15, 254) * mm});
            skLineSegment(sketch, "E238.MirrorCS", {"start": v(155.77, 254) * mm, "end": v(40.4, 387.35) * mm});
            skLineSegment(sketch, "E239.MirrorCS", {"start": v(155.77, 234.95) * mm, "end": v(155.77, 254) * mm});
            skLineSegment(sketch, "E240.MirrorCS", {"start": v(76.5, 19.05) * mm, "end": v(101.78, 66.36) * mm});
            skLineSegment(sketch, "E241.MirrorCS", {"start": v(72.14, 19.05) * mm, "end": v(72.14, 0) * mm});
            skLineSegment(sketch, "E242.MirrorCS", {"start": v(40.4, 19.05) * mm, "end": v(155.77, 234.95) * mm});
            skLineSegment(sketch, "E243.MirrorCS", {"start": v(76.5, 19.05) * mm, "end": v(603.86, 19.05) * mm, "construction": true});
            skLineSegment(sketch, "E244.MirrorCS", {"start": v(72.14, 0) * mm, "end": v(603.86, 0) * mm, "construction": true});
            skLineSegment(sketch, "E245.MirrorCS", {"start": v(40.4, 254) * mm, "end": v(603.86, 254) * mm, "construction": true});
            skLineSegment(sketch, "E246.MirrorCS", {"start": v(40.4, 234.95) * mm, "end": v(155.77, 234.95) * mm, "construction": true});
            skSolve(sketch);
        }
        {
            var Q0;
            Q0=makeQuery(id+"F14.imprint","IMPRINT",FACE,{"disambiguationData":[TD([[makeQuery(id+"F14.imprint","IMPRINT",EDGE,{"derivedFrom":sQuery(id+"F14.wireOp",EDGE,"E216.MirrorCS")}),1.0]])]});
            extrude(context, id + "F15", {"entities" : qUnion([Q0]), "endBound" : BoundingType.SYMMETRIC, "depth" : 19.05 * mm});
        }
        {
            var Q0;
            Q0=sQuery(id+"F0.wireOp",EDGE,"E98");
            cPlane(context, id + "F16", {"entities" : qUnion([Q0]), "cplaneType" : CPlaneType.LINE_ANGLE, "offset" : 25.4 * mm, "angle" : 0 * degree, "width" : 152.4 * mm, "height" : 152.4 * mm});
        }
        {
            var Q0;
            Q0=qCreatedBy(id+"F16.planeOp",FACE);
            var sketch = newSketch(context, id + "F17", { "sketchPlane" : qUnion([Q0])});
            skLineSegment(sketch, "E247", {"start": v(-442.84, 0) * mm, "end": v(-442.84, 406.4) * mm, "construction": true});
            skLineSegment(sketch, "E248.MirrorCS", {"start": v(-271.55, 254) * mm, "end": v(-273.32, 254) * mm});
            skLineSegment(sketch, "E249.MirrorCS", {"start": v(-109.72, 19.05) * mm, "end": v(-117.16, 19.05) * mm});
            skLineSegment(sketch, "E250.MirrorCS", {"start": v(-77.97, 19.05) * mm, "end": v(-77.97, 0) * mm});
            skLineSegment(sketch, "E251.MirrorCS", {"start": v(-109.72, 0) * mm, "end": v(-109.72, 19.05) * mm});
            skLineSegment(sketch, "E252.MirrorCS", {"start": v(-77.97, 0) * mm, "end": v(-109.72, 0) * mm});
            skLineSegment(sketch, "E253.MirrorCS", {"start": v(-194.11, 406.4) * mm, "end": v(-442.84, 406.4) * mm, "construction": true});
            skLineSegment(sketch, "E254.MirrorCS", {"start": v(-234.13, 254) * mm, "end": v(-150.99, 387.35) * mm});
            skLineSegment(sketch, "E255.MirrorCS", {"start": v(-150.99, 387.35) * mm, "end": v(-150.99, 406.4) * mm});
            skLineSegment(sketch, "E256.MirrorCS", {"start": v(-117.16, 19.05) * mm, "end": v(-273.32, 234.95) * mm});
            skLineSegment(sketch, "E257.MirrorCS", {"start": v(-77.97, 19.05) * mm, "end": v(-234.13, 234.95) * mm});
            skLineSegment(sketch, "E258.MirrorCS", {"start": v(-188.4, 387.35) * mm, "end": v(-188.4, 406.4) * mm});
            skLineSegment(sketch, "E259.MirrorCS", {"start": v(-77.97, 234.95) * mm, "end": v(-442.84, 234.95) * mm, "construction": true});
            skLineSegment(sketch, "E260.MirrorCS", {"start": v(-150.99, 406.4) * mm, "end": v(-188.4, 406.4) * mm});
            skLineSegment(sketch, "E261.MirrorCS", {"start": v(-77.97, 387.35) * mm, "end": v(-442.84, 387.35) * mm, "construction": true});
            skLineSegment(sketch, "E262.MirrorCS", {"start": v(-77.97, 0) * mm, "end": v(-442.84, 0) * mm, "construction": true});
            skLineSegment(sketch, "E263.MirrorCS", {"start": v(-77.97, 254) * mm, "end": v(-442.84, 254) * mm, "construction": true});
            skLineSegment(sketch, "E264.MirrorCS", {"start": v(-77.97, 406.4) * mm, "end": v(-150.99, 406.4) * mm, "construction": true});
            skLineSegment(sketch, "E265.MirrorCS", {"start": v(-77.97, 0) * mm, "end": v(-77.97, 406.4) * mm, "construction": true});
            skLineSegment(sketch, "E266.MirrorCS", {"start": v(-298.23, 0) * mm, "end": v(-298.23, 406.4) * mm, "construction": true});
            skLineSegment(sketch, "E267.MirrorCS", {"start": v(-273.32, 234.95) * mm, "end": v(-273.32, 254) * mm});
            skLineSegment(sketch, "E268.MirrorCS", {"start": v(-234.13, 234.95) * mm, "end": v(-234.13, 254) * mm});
            skLineSegment(sketch, "E269.MirrorCS", {"start": v(-271.55, 254) * mm, "end": v(-188.4, 387.35) * mm});
            skSolve(sketch);
        }
        {
            var Q0;
            Q0=makeQuery(id+"F17.imprint","IMPRINT",FACE,{"disambiguationData":[TD([[makeQuery(id+"F17.imprint","IMPRINT",EDGE,{"derivedFrom":sQuery(id+"F17.wireOp",EDGE,"E248.MirrorCS")}),1.0]])]});
            extrude(context, id + "F18", {"entities" : qUnion([Q0]), "endBound" : BoundingType.SYMMETRIC, "depth" : 19.05 * mm});
        }
        {
            var Q0;
            Q0=sQuery(id+"F0.wireOp",EDGE,"E100");
            cPlane(context, id + "F19", {"entities" : qUnion([Q0]), "cplaneType" : CPlaneType.LINE_ANGLE, "offset" : 25.4 * mm, "angle" : 90 * degree, "width" : 152.4 * mm, "height" : 152.4 * mm});
        }
        {
            var Q0;
            Q0=qCreatedBy(id+"F19.planeOp",FACE);
            var sketch = newSketch(context, id + "F20", { "sketchPlane" : qUnion([Q0])});
            skLineSegment(sketch, "E270", {"start": v(77.67, 0) * mm, "end": v(77.67, 406.4) * mm, "construction": true});
            skLineSegment(sketch, "E271", {"start": v(442.55, 0) * mm, "end": v(442.55, 406.4) * mm, "construction": true});
            skLineSegment(sketch, "E272", {"start": v(297.94, 0) * mm, "end": v(297.94, 406.4) * mm, "construction": true});
            skLineSegment(sketch, "E273", {"start": v(77.67, 406.4) * mm, "end": v(150.69, 406.4) * mm, "construction": true});
            skLineSegment(sketch, "E274", {"start": v(77.67, 254) * mm, "end": v(442.55, 254) * mm, "construction": true});
            skLineSegment(sketch, "E275", {"start": v(77.67, 0) * mm, "end": v(442.55, 0) * mm, "construction": true});
            skLineSegment(sketch, "E276.0", {"start": v(77.67, 387.35) * mm, "end": v(442.55, 387.35) * mm, "construction": true});
            skLineSegment(sketch, "E277.0", {"start": v(29.78, 234.95) * mm, "end": v(517.75, 234.95) * mm, "construction": true});
            skLineSegment(sketch, "E278", {"start": v(77.67, 0) * mm, "end": v(109.42, 0) * mm});
            skLineSegment(sketch, "E279", {"start": v(109.42, 0) * mm, "end": v(109.42, 19.05) * mm});
            skLineSegment(sketch, "E280", {"start": v(77.67, 19.05) * mm, "end": v(77.67, 0) * mm});
            skLineSegment(sketch, "E281", {"start": v(77.67, 19.05) * mm, "end": v(233.84, 234.95) * mm});
            skLineSegment(sketch, "E282.0", {"start": v(116.86, 19.05) * mm, "end": v(273.02, 234.95) * mm});
            skLineSegment(sketch, "E283", {"start": v(109.42, 19.05) * mm, "end": v(116.86, 19.05) * mm});
            skLineSegment(sketch, "E284", {"start": v(233.84, 234.95) * mm, "end": v(233.84, 254) * mm});
            skLineSegment(sketch, "E285", {"start": v(273.02, 234.95) * mm, "end": v(273.02, 254) * mm});
            skLineSegment(sketch, "E286", {"start": v(233.84, 254) * mm, "end": v(150.69, 387.35) * mm});
            skLineSegment(sketch, "E287.0", {"start": v(271.25, 254) * mm, "end": v(188.1, 387.35) * mm});
            skLineSegment(sketch, "E288", {"start": v(150.69, 387.35) * mm, "end": v(150.69, 406.4) * mm});
            skLineSegment(sketch, "E289", {"start": v(188.1, 387.35) * mm, "end": v(188.1, 406.4) * mm});
            skLineSegment(sketch, "E290.trimOffspring", {"start": v(193.81, 406.4) * mm, "end": v(442.55, 406.4) * mm, "construction": true});
            skLineSegment(sketch, "E291", {"start": v(150.69, 406.4) * mm, "end": v(188.1, 406.4) * mm});
            skLineSegment(sketch, "E292", {"start": v(271.25, 254) * mm, "end": v(273.02, 254) * mm});
            skSolve(sketch);
        }
        {
            var Q0;
            Q0=makeQuery(id+"F20.imprint","IMPRINT",FACE,{"disambiguationData":[TD([[makeQuery(id+"F20.imprint","IMPRINT",EDGE,{"derivedFrom":sQuery(id+"F20.wireOp",EDGE,"E278")}),1.0]])]});
            extrude(context, id + "F21", {"entities" : qUnion([Q0]), "endBound" : BoundingType.SYMMETRIC, "depth" : 19.05 * mm});
        }
    });
